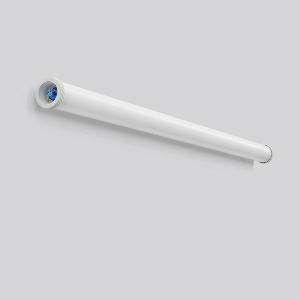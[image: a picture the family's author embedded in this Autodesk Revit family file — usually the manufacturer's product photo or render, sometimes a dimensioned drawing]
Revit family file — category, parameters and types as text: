
# Revit family: planox_tube_farm_601072_002_5_84f7
name_source: partatom
category: Lighting Fixtures
units: mm (PartAtom-declared; Revit-internal decimal feet)

## family parameters
Cut with Voids When Loaded = No
Host = Face
Light Source = No
Part Type = Normal
Room Calculation Point = No
Round Connector Dimension = Use Diameter
Shared = No

## types (1)
- PLANOX TUBE FARM (1 x LED Modul 840, 10000 lm, 4000)
    Apparent Load = 62 VA
    CIE Flux Codes = 44 74 91 92 100
    Color Rendering = 80
    Color Temperature = 4000
    Default Elevation = 1800 mm
    Description = Series: PLANOX TUBE FARM
Ammonia-resistant protective tube luminaire for tough requirements. Rack made of sheet steel, white powder coated. End caps made of plastic (polyamide) grey. Diffuser made of UV-resistant plastic (PMMA), opal. Symmetrical light distribution. Homogeneous light distribution. With accessories for wall, ceiling or pendant mounting. Driver integrated. Easy installation with the Plug+Play Wieland RST CLASSIC plug-in system. Mounting set must be ordered separately. Luminaire with limited surface temperature in accordance with EN 60598-2-24 for use in environments in which a deposit of conductive dust on the luminaire can be expected. Ammonia resistant : Suitable for the use in stables with livestock and agricultural side areas. Environmentally friendly and resource-saving due to replaceable components. 
Colour: white
Diameter: 78 mm
Length: 1564 mm
Lamp: LED
Socket: without socket
Colour temperature: 4000K
Colour rendering index (CRI): 83
System power: 62 W
Rated luminous flux: 10000 lm
Luminous efficiency: 161 lm/W
Control gear: Regulated power supply
Protection class: I
Type of protection: IP 67
    Height = 0 mm  [stored 0 ft]
    Lamp = 1 x LED Modul 840
    Lamp Light Flux = 10000 lm
    Lamp count = 1
    Length = 1564 mm
    Lifetime = 50000 h
    Luminous efficacy = 161 lm/W
    Manufacturer = RZB
    ModVariant = No
    Model = 601072.002.5
    Mounting Place = Ceiling
    Mounting Type = Surface mounted
    Number of Poles = 1
    OnlyDefault = Yes
    Power Factor = 1
    Product Name = PLANOX TUBE FARM
    Product group = Surface mounted luminaires for moist/humid enviroments
    ProductGroupID = 308
    Protection Class = Protection class I
    Protection Degree = Degree of protection
    RLX_Detail_Level = 1
    RLX_Emergency_Light_Flux = 0 lm
    RLX_Emergency_Type = 0
    RLX_Emergency_Type_DB = No
    RlxData = <blob elided: 34437 chars, md5=80ba8233>
    Socket = socket
    Standby Power = 0 W
    System Light Flux = 10000 lm
    System Power = 62 W
    Type Comments = Product without accessories
    Type Image = 601072.002.5.jpg
    URL = http://relux.com
    VarID = ---
    Voltage = 0 V
    Weight = 0.00 kg
    Width = 0 mm  [stored 0 ft]

note: [stored X ft] marks values corroborated as IEEE doubles in the binary element streams (Revit-internal decimal feet)

## geometry (parser evidence)
native form markers: Blend x4, Sweep x10
no freeform markers — native parametric forms only
